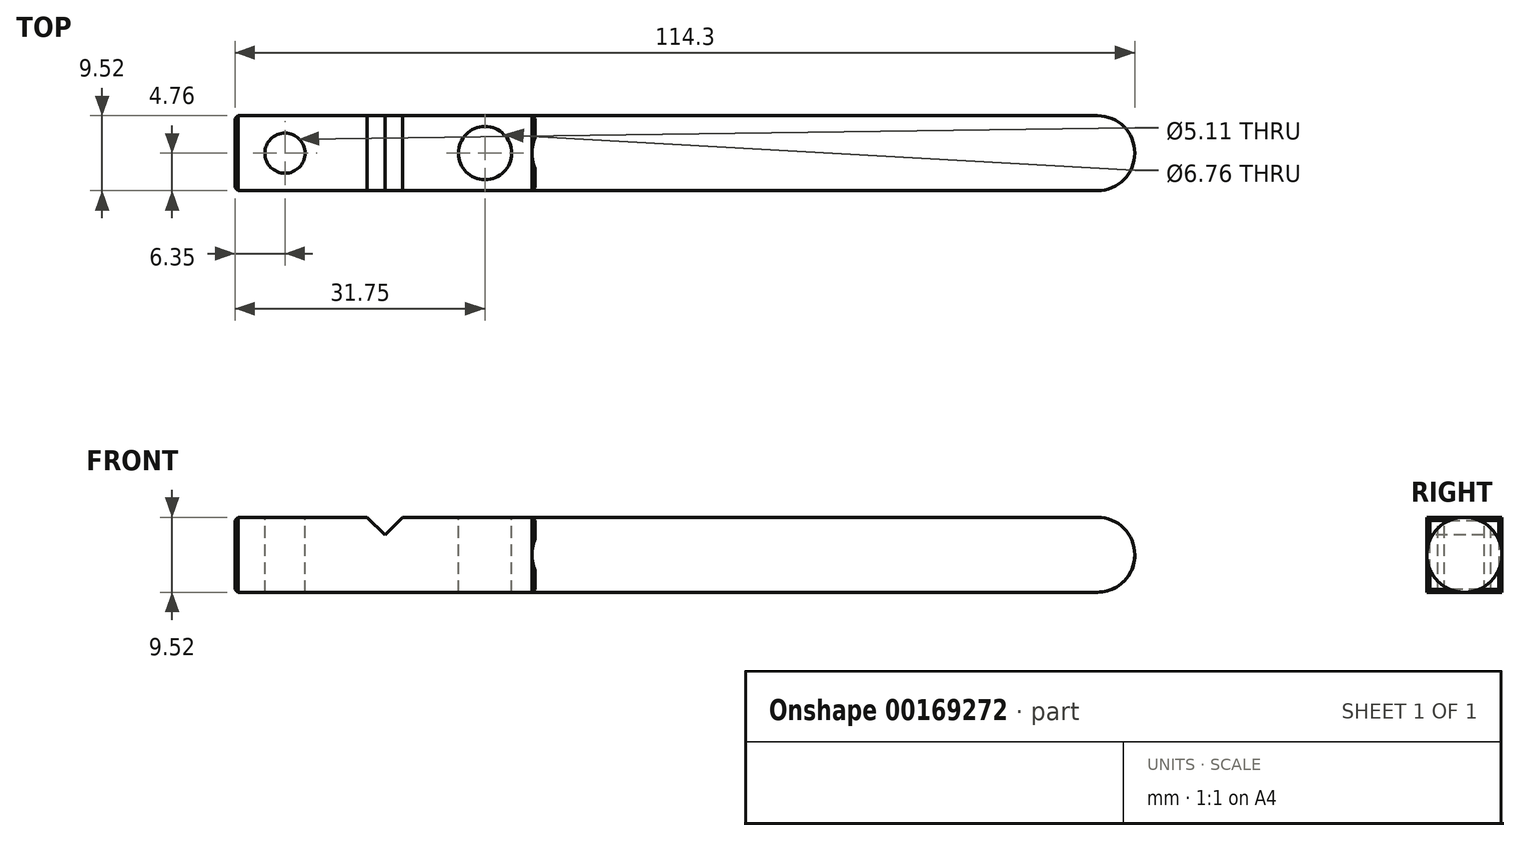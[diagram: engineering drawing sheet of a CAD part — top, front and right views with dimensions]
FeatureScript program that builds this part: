
annotation { "Feature Type Name" : "Feature", "Feature Type Description" : "" }
export const myFeature = defineFeature(function(context is Context, id is Id, definition is map)
    precondition{}
    {
        {
            var Q0;
            Q0=qCreatedBy(makeId("Top.planeOp"),FACE);
            var sketch = newSketch(context, id + "F0", { "sketchPlane" : qUnion([Q0])});
            skLineSegment(sketch, "E0.bottom", {"start": v(-19.05, 4.76) * mm, "end": v(19.05, 4.76) * mm});
            skLineSegment(sketch, "E0.top", {"start": v(-19.05, -4.76) * mm, "end": v(19.05, -4.76) * mm});
            skLineSegment(sketch, "E0.left", {"start": v(-19.05, 4.76) * mm, "end": v(-19.05, -4.76) * mm});
            skLineSegment(sketch, "E0.right", {"start": v(19.05, 4.76) * mm, "end": v(19.05, -4.76) * mm});
            skSolve(sketch);
        }
        {
            var Q0;
            Q0=makeQuery(id+"F0.imprint","IMPRINT",FACE,{"disambiguationData":[TD([[makeQuery(id+"F0.imprint","IMPRINT",EDGE,{"derivedFrom":sQuery(id+"F0.wireOp",EDGE,"E0.bottom")}),-1.0]])]});
            extrude(context, id + "F1", {"entities" : qUnion([Q0]), "endBound" : BoundingType.SYMMETRIC, "depth" : 9.52 * mm});
        }
        {
            var Q0;
            Q0=makeQuery(id+"F1.opExtrude","SWEPT_FACE",FACE,{"disambiguationData":[OSD([sQuery(id+"F0.wireOp",EDGE,"E0.right")])]});
            var sketch = newSketch(context, id + "F2", { "sketchPlane" : qUnion([Q0])});
            skCircle(sketch, "E1", {"center": v(0, 0) * mm, "radius": 4.76 * mm});
            skSolve(sketch);
        }
        {
            var Q0;
            {var subQ0=sQuery(id+"F2.wireOp",EDGE,"E1");var subQ1=sQuery(id+"F0.wireOp",EDGE,"E0.right");var subQ2=makeQuery(id+"F2.imprint","INTERSECT",VERTEX,{"derivedFrom":[makeQuery(id+"F1.opExtrude","CAP_EDGE",EDGE,{"disambiguationData":[OSD([subQ1])],"isStart":false}),subQ0]});Q0=makeQuery(id+"F2.imprint","IMPRINT",FACE,{"disambiguationData":[TD([[makeQuery(id+"F2.imprint","IMPRINT",EDGE,{"disambiguationData":[TD([[subQ2,1.0]])],"derivedFrom":subQ0}),1.0]])]});}
            extrude(context, id + "F3", {"entities" : qUnion([Q0]), "operationType" : NewBodyOperationType.ADD, "depth" : 76.2 * mm});
        }
        {
            var Q0;
            Q0=makeQuery(id+"F3.opExtrude","CAP_FACE",FACE,{"disambiguationData":[OSD([sQuery(id+"F2.wireOp",EDGE,"E1")])],"isStart":false});
            fillet(context, id + "F4", {"entities" : qUnion([Q0]), "radius" : 4.76 * mm, "tangentPropagation" : true, "allowEdgeOverflow" : false});
        }
        {
            var Q0;
            Q0=makeQuery(id+"F1.opExtrude","CAP_FACE",FACE,{"disambiguationData":[OSD([sQuery(id+"F0.wireOp",EDGE,"E0.bottom"),sQuery(id+"F0.wireOp",EDGE,"E0.top"),sQuery(id+"F0.wireOp",EDGE,"E0.left"),sQuery(id+"F0.wireOp",EDGE,"E0.right")])],"isStart":false});
            var sketch = newSketch(context, id + "F5", { "sketchPlane" : qUnion([Q0])});
            skCircle(sketch, "E2", {"center": v(-12.7, 0) * mm, "radius": 2.98 * mm});
            skSolve(sketch);
        }
        {
            var Q0;
            Q0=sQuery(id+"F5.wireOp",VERTEX,"E2.center");
            var Q1;
            Q1=makeQuery(id+"F1.opExtrude","SWEPT_BODY",BODY,{"disambiguationData":[OSD([sQuery(id+"F0.wireOp",EDGE,"E0.bottom"),sQuery(id+"F0.wireOp",EDGE,"E0.top"),sQuery(id+"F0.wireOp",EDGE,"E0.left"),sQuery(id+"F0.wireOp",EDGE,"E0.right")])]});
            hole(context, id + "F6", {"style" : HoleStyle.SIMPLE, "endStyle" : HoleEndStyle.THROUGH, "standardTappedOrClearance" : lookupTablePath({ "standard" : "ANSI", "engagement" : "75%", "pitch" : "20 tpi", "size" : "1/4", "type" : "Tapped" }), "standardBlindInLast" : lookupTablePath({ "standard" : "ANSI", "engagement" : "75%", "pitch" : "20 tpi", "size" : "1/4", "type" : "Tapped" }), "holeDiameter" : 5.1 * mm, "locations" : qUnion([Q0]), "scope" : qUnion([Q1]), "isTappedThrough" : true, "majorDiameter" : 6.35 * mm, "showTappedDepth" : true});
        }
        {
            var Q0;
            Q0=makeQuery(id+"F1.opExtrude","CAP_FACE",FACE,{"disambiguationData":[OSD([sQuery(id+"F0.wireOp",EDGE,"E0.bottom"),sQuery(id+"F0.wireOp",EDGE,"E0.top"),sQuery(id+"F0.wireOp",EDGE,"E0.left"),sQuery(id+"F0.wireOp",EDGE,"E0.right")])],"isStart":false});
            var sketch = newSketch(context, id + "F7", { "sketchPlane" : qUnion([Q0])});
            skCircle(sketch, "E3", {"center": v(12.7, 0) * mm, "radius": 3.88 * mm});
            skSolve(sketch);
        }
        {
            var Q0;
            Q0=sQuery(id+"F7.wireOp",VERTEX,"E3.center");
            var Q1;
            Q1=makeQuery(id+"F1.opExtrude","SWEPT_BODY",BODY,{"disambiguationData":[OSD([sQuery(id+"F0.wireOp",EDGE,"E0.bottom"),sQuery(id+"F0.wireOp",EDGE,"E0.top"),sQuery(id+"F0.wireOp",EDGE,"E0.left"),sQuery(id+"F0.wireOp",EDGE,"E0.right")])]});
            hole(context, id + "F8", {"style" : HoleStyle.SIMPLE, "endStyle" : HoleEndStyle.THROUGH, "standardTappedOrClearance" : lookupTablePath({ "standard" : "ANSI", "fit" : "Normal (ASME)", "size" : "1/4", "type" : "Clearance" }), "standardBlindInLast" : lookupTablePath({ "fit" : "Free", "standard" : "ANSI", "size" : "1/4", "type" : "Clearance" }), "holeDiameter" : 6.76 * mm, "locations" : qUnion([Q0]), "scope" : qUnion([Q1]), "isTappedThrough" : true});
        }
        {
            var Q0;
            Q0=makeQuery(id+"F1.opExtrude","SWEPT_FACE",FACE,{"disambiguationData":[OSD([sQuery(id+"F0.wireOp",EDGE,"E0.top")])]});
            var sketch = newSketch(context, id + "F9", { "sketchPlane" : qUnion([Q0])});
            skLineSegment(sketch, "E4", {"start": v(-2.25, 4.76) * mm, "end": v(0, 2.52) * mm});
            skLineSegment(sketch, "E5", {"start": v(0, 2.52) * mm, "end": v(2.25, 4.76) * mm});
            skLineSegment(sketch, "E6", {"start": v(2.25, 4.76) * mm, "end": v(-2.25, 4.76) * mm});
            skSolve(sketch);
        }
        {
            var Q0;
            Q0=makeQuery(id+"F9.imprint","IMPRINT",FACE,{"disambiguationData":[TD([[makeQuery(id+"F9.imprint","IMPRINT",EDGE,{"derivedFrom":sQuery(id+"F9.wireOp",EDGE,"E4")}),1.0]])]});
            extrude(context, id + "F10", {"entities" : qUnion([Q0]), "operationType" : NewBodyOperationType.REMOVE, "oppositeDirection" : true, "depth" : 25.4 * mm});
        }
        {
            var Q0;
            Q0=makeQuery(id+"F1.opExtrude","SWEPT_FACE",FACE,{"disambiguationData":[OSD([sQuery(id+"F0.wireOp",EDGE,"E0.left")])]});
            var Q1;
            {var subQ0=sQuery(id+"F0.wireOp",EDGE,"E0.right");var subQ1=sQuery(id+"F0.wireOp",EDGE,"E0.top");Q1=makeQuery(id+"F3.boolean.opBoolean","SPLIT",EDGE,{"disambiguationData":[TD([makeQuery(id+"F1.opExtrude","CAP_FACE",FACE,{"disambiguationData":[OSD([sQuery(id+"F0.wireOp",EDGE,"E0.bottom"),subQ1,sQuery(id+"F0.wireOp",EDGE,"E0.left"),subQ0])],"isStart":false})])],"derivedFrom":makeQuery(id+"F1.opExtrude","SWEPT_EDGE",EDGE,{"disambiguationData":[OSD([subQ1,subQ0])]})});}
            var Q2;
            {var subQ0=sQuery(id+"F0.wireOp",EDGE,"E0.right");var subQ1=sQuery(id+"F0.wireOp",EDGE,"E0.top");Q2=makeQuery(id+"F3.boolean.opBoolean","SPLIT",EDGE,{"disambiguationData":[TD([makeQuery(id+"F1.opExtrude","SWEPT_FACE",FACE,{"disambiguationData":[OSD([subQ1])]})])],"derivedFrom":makeQuery(id+"F1.opExtrude","CAP_EDGE",EDGE,{"disambiguationData":[OSD([subQ0])],"isStart":false})});}
            var Q3;
            Q3=makeQuery(id+"F8.hole-0.boolean.opBoolean","INTERSECT",EDGE,{"derivedFrom":[makeQuery(id+"F1.opExtrude","CAP_FACE",FACE,{"disambiguationData":[OSD([sQuery(id+"F0.wireOp",EDGE,"E0.bottom"),sQuery(id+"F0.wireOp",EDGE,"E0.top"),sQuery(id+"F0.wireOp",EDGE,"E0.left"),sQuery(id+"F0.wireOp",EDGE,"E0.right")])],"isStart":true}),makeQuery(id+"F8.hole-0.opRevolve","SWEPT_FACE",FACE,{"disambiguationData":[OSD([sQuery(id+"F8.hole-0.sketch.wireOp",EDGE,"core_line_2")])]})]});
            var Q4;
            {var subQ0=sQuery(id+"F0.wireOp",EDGE,"E0.right");var subQ1=sQuery(id+"F0.wireOp",EDGE,"E0.top");Q4=makeQuery(id+"F3.boolean.opBoolean","SPLIT",EDGE,{"disambiguationData":[TD([makeQuery(id+"F1.opExtrude","SWEPT_FACE",FACE,{"disambiguationData":[OSD([subQ1])]})])],"derivedFrom":makeQuery(id+"F1.opExtrude","CAP_EDGE",EDGE,{"disambiguationData":[OSD([subQ0])],"isStart":true})});}
            var Q5;
            {var subQ0=sQuery(id+"F0.wireOp",EDGE,"E0.bottom");var subQ1=sQuery(id+"F0.wireOp",EDGE,"E0.right");Q5=makeQuery(id+"F3.boolean.opBoolean","SPLIT",EDGE,{"disambiguationData":[TD([makeQuery(id+"F1.opExtrude","CAP_FACE",FACE,{"disambiguationData":[OSD([subQ0,sQuery(id+"F0.wireOp",EDGE,"E0.top"),sQuery(id+"F0.wireOp",EDGE,"E0.left"),subQ1])],"isStart":false})])],"derivedFrom":makeQuery(id+"F1.opExtrude","SWEPT_EDGE",EDGE,{"disambiguationData":[OSD([subQ0,subQ1])]})});}
            var Q6;
            Q6=makeQuery(id+"F8.hole-0.boolean.opBoolean","COPY",EDGE,{"derivedFrom":makeQuery(id+"F8.hole-0.opRevolve","SWEPT_EDGE",EDGE,{"disambiguationData":[OSD([sQuery(id+"F8.hole-0.sketch.wireOp",EDGE,"core_line_2"),sQuery(id+"F8.hole-0.sketch.wireOp",EDGE,"core_line_3")])]})});
            var Q7;
            Q7=makeQuery(id+"F6.hole-0.boolean.opBoolean","COPY",EDGE,{"derivedFrom":makeQuery(id+"F6.hole-0.opRevolve","SWEPT_EDGE",EDGE,{"disambiguationData":[OSD([sQuery(id+"F6.hole-0.sketch.wireOp",EDGE,"core_line_2"),sQuery(id+"F6.hole-0.sketch.wireOp",EDGE,"core_line_3")])]})});
            var Q8;
            Q8=makeQuery(id+"F6.hole-0.boolean.opBoolean","INTERSECT",EDGE,{"derivedFrom":[makeQuery(id+"F1.opExtrude","CAP_FACE",FACE,{"disambiguationData":[OSD([sQuery(id+"F0.wireOp",EDGE,"E0.bottom"),sQuery(id+"F0.wireOp",EDGE,"E0.top"),sQuery(id+"F0.wireOp",EDGE,"E0.left"),sQuery(id+"F0.wireOp",EDGE,"E0.right")])],"isStart":true}),makeQuery(id+"F6.hole-0.opRevolve","SWEPT_FACE",FACE,{"disambiguationData":[OSD([sQuery(id+"F6.hole-0.sketch.wireOp",EDGE,"core_line_2")])]})]});
            chamfer(context, id + "F11", {"entities" : qUnion([Q0, Q1, Q2, Q3, Q4, Q5, Q6, Q7, Q8]), "width" : 0.38 * mm, "tangentPropagation" : true});
        }
    });
